# Revit family: ONIZGGA - Low Temp Closed
name_source: partatom
category: Mechanical Equipment
units: mm (PartAtom-declared; Revit-internal decimal feet)

## family parameters
Always vertical = Yes
Cut with Voids When Loaded = No
OmniClass Number = 23.40.40.11.17
OmniClass Title = Refrigerated Cases
Part Type = Normal
Room Calculation Point = No
Round Connector Dimension = Use Radius
Shared = No
Work Plane-Based = Yes

## types (4) — shared parameters
Anti-Condensate Heaters Amps = 0 A
Anti-Condensate Heaters Watts = 0 W
BOTTOM ELECTRICAL = Yes
BOTTOM REFRIGERATION PIPING = Yes
Certifications = NSF 7, UL471, CSA
Condensing  Data Volts = 0 V
Condensing Frequency (Hz) = 0 Hz
DATE = 04/15/2016
DRAIN PIPING = Yes
Default Elevation = 48"
Description = ONIZGGA - Island case
Discharge Air (°F) = -460 °F
Discharge Air Velocity (FPM) = 0 FPM
EQUIPMENT DESCRIPTION = ONIZGGA - Island case
EQUIPMENT MARK = ONIZGGA
Electric Defrost Termination Temp (°F) = -460 °F
Evaporator Pan Heater  Amps = 0 A
Evaporator Pan Heater  Watts = 0 W
GLASS = Glass
Height = 38 1/8"
High Efficiency Amps = 0 A
High Efficiency Watts = 0 W
Item Description = ONIZGGA - Island case
LF STD END = Yes
Legend Number = ONIZGGA
Length of Cases = 0"
Locked Rotor (LRA) Amps = 0 A
Manufacturer = HILL PHOENIX
Maximum Overcurrent Protection = 0 A
Minimum Circuit Ampacity = 0 A
Model = ONIZGGA
PAINTED METAL UPPER SHELF = PAINTED SHELVES
REAR REFRIGERATION PIPING = Yes
REFRIGERATION PIPING = COPPER PIPE
RT STD END = Yes
Running Load (RLA) Amps = 0 A
STAINLESS STEEL = GALVANIZED STEEL
Suction Pressure @ Case Outlet (psig) = 0.00 psi
Systems Frequency (Hz) = 0 Hz
Systems Volts = 0 V
TOP ELECTRICAL = Yes
TOP REFRIGERATION PIPING = Yes
Timed-Off Defrost Termination Temp = -460 °F
URL = http://www.hillphoenix.com
Width = 44 1/8"
zero-valued in all types: Condensing Data  Phase, Defrosts Per Day, Lbs. of Refrigerant, Number of Fans, Systems Phase

## per-type parameters (varying)
| type | CENTER LINE | Length |
| 05' | 33 13/16" | 67 5/8" |
| 06' | 39 13/16" | 79 5/8" |
| 08' | 51 13/16" | 103 5/8" |
| 12' | 75 13/16" | 151 5/8" |

## geometry (parser evidence)
native form markers: Blend x8, Sweep x2
no freeform markers — native parametric forms only
